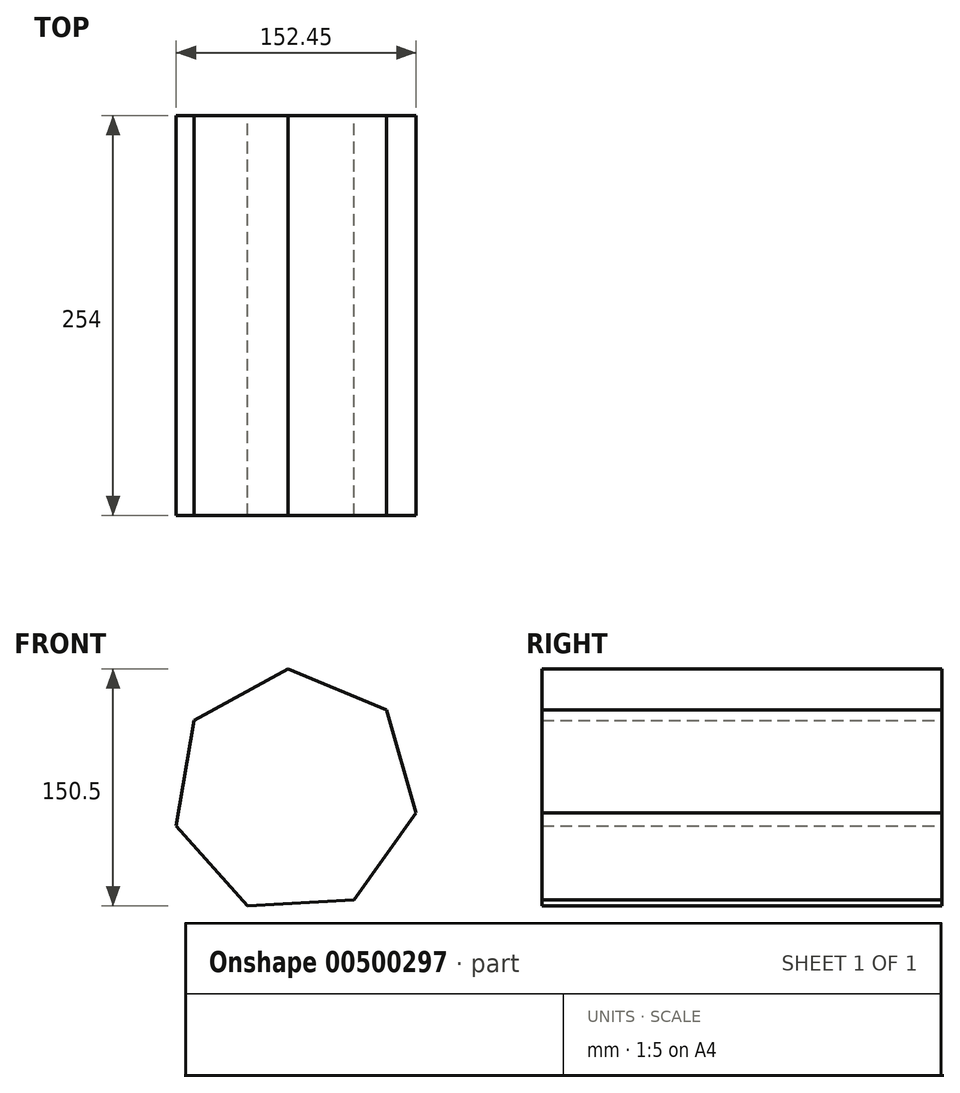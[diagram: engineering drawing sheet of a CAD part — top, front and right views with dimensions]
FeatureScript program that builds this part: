
annotation { "Feature Type Name" : "Feature", "Feature Type Description" : "" }
export const myFeature = defineFeature(function(context is Context, id is Id, definition is map)
    precondition{}
    {
        {
            var Q0;
            Q0=qCreatedBy(makeId("Front.planeOp"),FACE);
            var sketch = newSketch(context, id + "F0", { "sketchPlane" : qUnion([Q0])});
            skCircle(sketch, "E0.cCircle", {"center": v(0, 2.04) * mm, "radius": 78.3 * mm, "construction": true});
            skLineSegment(sketch, "E0.0", {"start": v(-63.83, 47.4) * mm, "end": v(-4.34, 80.22) * mm});
            skLineSegment(sketch, "E0.1", {"start": v(-4.34, 80.22) * mm, "end": v(58.42, 54.18) * mm});
            skLineSegment(sketch, "E0.2", {"start": v(58.42, 54.18) * mm, "end": v(77.19, -11.13) * mm});
            skLineSegment(sketch, "E0.3", {"start": v(77.19, -11.13) * mm, "end": v(37.83, -66.52) * mm});
            skLineSegment(sketch, "E0.4", {"start": v(37.83, -66.52) * mm, "end": v(-30.02, -70.28) * mm});
            skLineSegment(sketch, "E0.5", {"start": v(-30.02, -70.28) * mm, "end": v(-75.26, -19.59) * mm});
            skLineSegment(sketch, "E0.6", {"start": v(-75.26, -19.59) * mm, "end": v(-63.83, 47.4) * mm});
            skSolve(sketch);
        }
        {
            var Q0;
            Q0=makeQuery(id+"F0.imprint","IMPRINT",FACE,{"disambiguationData":[TD([[makeQuery(id+"F0.imprint","IMPRINT",EDGE,{"derivedFrom":sQuery(id+"F0.wireOp",EDGE,"E0.0")}),-1.0]])]});
            extrude(context, id + "F1", {"entities" : qUnion([Q0]), "endBound" : BoundingType.SYMMETRIC, "depth" : 254 * mm});
        }
    });
